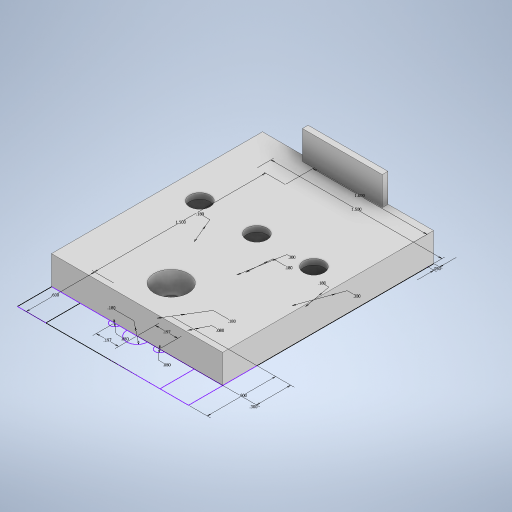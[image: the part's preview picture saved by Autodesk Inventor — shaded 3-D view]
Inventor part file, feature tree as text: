
AUTODESK INVENTOR PART (.ipt)
format: ipt  version: 2024.2 (Build 282272000, 272)  size: 315,392 bytes
history: native  units: in
note: dims shown in document units (in); Inventor stores cm internally (conversion verified against a paired STEP export)
features: extrude x6, sketch x5
ambient origin geometry x8: Origin, YZ Plane, XZ Plane, XY Plane, X Axis, Y Axis, Z Axis, Center Point
bodies: Solid1 (feature_tree)
feature tree (11):
  sketch  "Sketch1"  dims[d0=1.5in d1=1.0in]
  extrude  "Extrusion1"  Depth=1.5in
  extrude  "Extrusion2"  Depth=0.6in
  extrude  "Extrusion3"  Depth=1.5in
  extrude  "Extrusion4"  Depth=0.18in
  sketch  "Sketch3"  dims[d4=1.5in d5=0.18in]
  extrude  "Extrusion5"  Depth=0.05in
  sketch  "Sketch4"  dims[d6=0.18in d7=0.18in]
  extrude  "Extrusion6"  Depth=0.5in TaperAngle=0.0deg
  sketch  "Sketch2"  dims[d2=0.18in d3=0.6in]
  sketch  "Sketch5"  dims[d8=0.25in d9=0.0in d10=0.05in d11=0.5in d12=0.0in d13=0.6in d14=0.3in d15=0.3in d16=0.3in d17=0.2in d18=0.0in d19=0.3in d20=0.2in d21=0.0in d22=0.197in d23=0.197in d24=0.08in d25=0.08in d26=0.175in d27=0.0in d28=0.18in d29=0.08in d30=0.4in d31=0.4in d32=0.25in d33=1.0in d34=0.0in]
